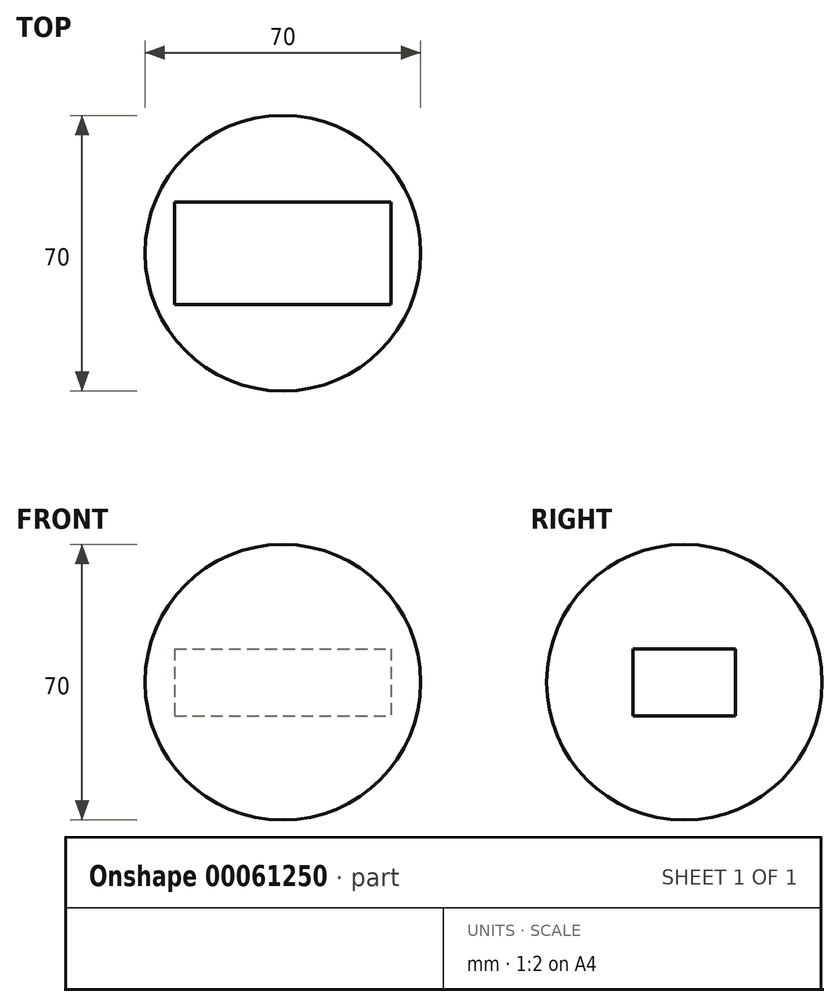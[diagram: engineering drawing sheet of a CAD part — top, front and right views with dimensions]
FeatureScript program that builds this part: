
annotation { "Feature Type Name" : "Feature", "Feature Type Description" : "" }
export const myFeature = defineFeature(function(context is Context, id is Id, definition is map)
    precondition{}
    {
        {
            var Q0;
            Q0=qCreatedBy(makeId("Top.planeOp"),FACE);
            var sketch = newSketch(context, id + "F0", { "sketchPlane" : qUnion([Q0])});
            skLineSegment(sketch, "E0.bottom", {"start": v(-27.5, 13) * mm, "end": v(27.5, 13) * mm});
            skLineSegment(sketch, "E0.top", {"start": v(-27.5, -13) * mm, "end": v(27.5, -13) * mm});
            skLineSegment(sketch, "E0.left", {"start": v(-27.5, 13) * mm, "end": v(-27.5, -13) * mm});
            skLineSegment(sketch, "E0.right", {"start": v(27.5, 13) * mm, "end": v(27.5, -13) * mm});
            skPoint(sketch, "E1", {"position": v(0, 13) * mm});
            skPoint(sketch, "E2", {"position": v(27.5, 0) * mm});
            skSolve(sketch);
        }
        {
            var Q0;
            Q0 = qSketchRegion(id + "F0", true);
            extrude(context, id + "F1", {"entities" : qUnion([Q0]), "endBound" : BoundingType.SYMMETRIC, "depth" : 17 * mm});
        }
        {
            var Q0;
            Q0=qCreatedBy(makeId("Top.planeOp"),FACE);
            var sketch = newSketch(context, id + "F2", { "sketchPlane" : qUnion([Q0])});
            skArc(sketch, "E3", {"start": v(0, 35) * mm, "mid": v(-35, 0) * mm, "end": v(0, -35) * mm});
            skLineSegment(sketch, "E4", {"start": v(0, 35) * mm, "end": v(0, -35) * mm});
            skSolve(sketch);
        }
        {
            var Q0;
            Q0 = qSketchRegion(id + "F2", true);
            var Q1;
            Q1=sQuery(id+"F2.wireOp",EDGE,"E4");
            revolve(context, id + "F3", {"entities" : qUnion([Q0]), "axis" : qUnion([Q1]), "revolveType" : RevolveType.FULL});
        }
    });
